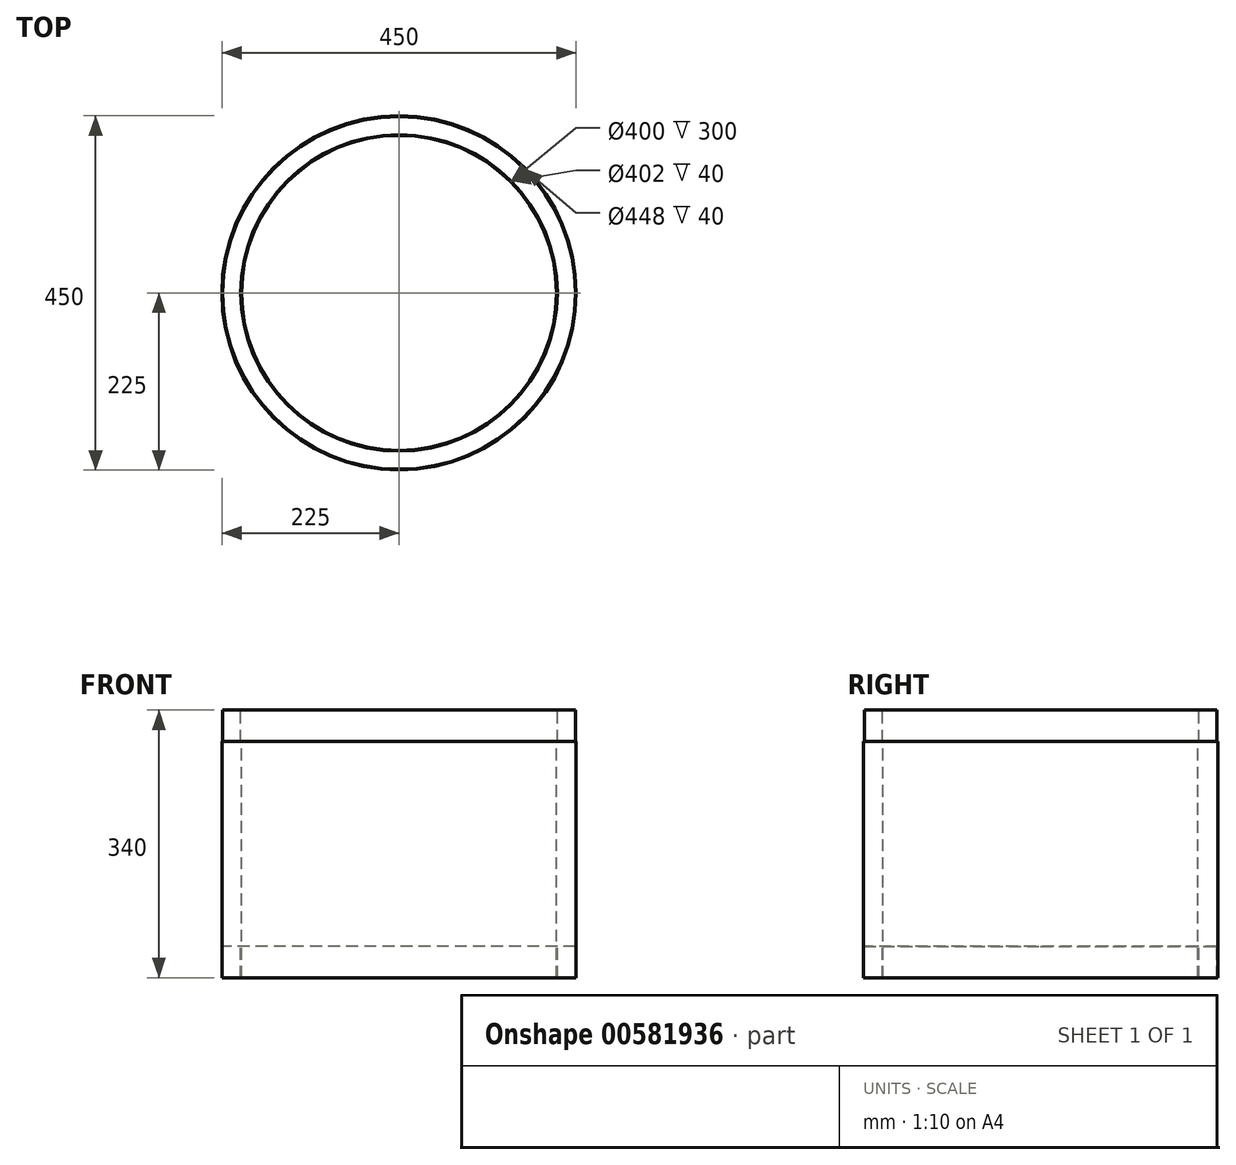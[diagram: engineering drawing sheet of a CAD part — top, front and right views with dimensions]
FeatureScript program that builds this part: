
annotation { "Feature Type Name" : "Feature", "Feature Type Description" : "" }
export const myFeature = defineFeature(function(context is Context, id is Id, definition is map)
    precondition{}
    {
        {
            var Q0;
            Q0=qCreatedBy(makeId("Front.planeOp"),FACE);
            var sketch = newSketch(context, id + "F0", { "sketchPlane" : qUnion([Q0])});
            skLineSegment(sketch, "E0", {"start": v(0, 345.75) * mm, "end": v(0, -558.03) * mm, "construction": true});
            skLineSegment(sketch, "E1", {"start": v(-200, -518.84) * mm, "end": v(-200, -218.84) * mm});
            skLineSegment(sketch, "E2", {"start": v(-200, -218.84) * mm, "end": v(-201, -218.84) * mm});
            skLineSegment(sketch, "E3", {"start": v(-201, -218.84) * mm, "end": v(-201, -178.84) * mm});
            skLineSegment(sketch, "E4", {"start": v(-201, -178.84) * mm, "end": v(-224, -178.84) * mm});
            skLineSegment(sketch, "E5", {"start": v(-224, -178.84) * mm, "end": v(-224, -218.84) * mm});
            skLineSegment(sketch, "E6", {"start": v(-224, -218.84) * mm, "end": v(-225, -218.84) * mm});
            skLineSegment(sketch, "E7", {"start": v(-225, -218.84) * mm, "end": v(-225, -518.84) * mm});
            skLineSegment(sketch, "E8", {"start": v(-225, -518.84) * mm, "end": v(-224, -518.84) * mm});
            skLineSegment(sketch, "E9", {"start": v(-224, -518.84) * mm, "end": v(-224, -478.84) * mm});
            skLineSegment(sketch, "E10", {"start": v(-224, -478.84) * mm, "end": v(-201, -478.84) * mm});
            skLineSegment(sketch, "E11", {"start": v(-201, -478.84) * mm, "end": v(-201, -518.84) * mm});
            skLineSegment(sketch, "E12", {"start": v(-201, -518.84) * mm, "end": v(-200, -518.84) * mm});
            skSolve(sketch);
        }
        {
            var Q0;
            Q0=qSketchRegion(id+"F0",true);
            var Q1;
            Q1=sQuery(id+"F0.wireOp",EDGE,"E0");
            revolve(context, id + "F1", {"entities" : qUnion([Q0]), "axis" : qUnion([Q1]), "revolveType" : RevolveType.FULL});
        }
    });
